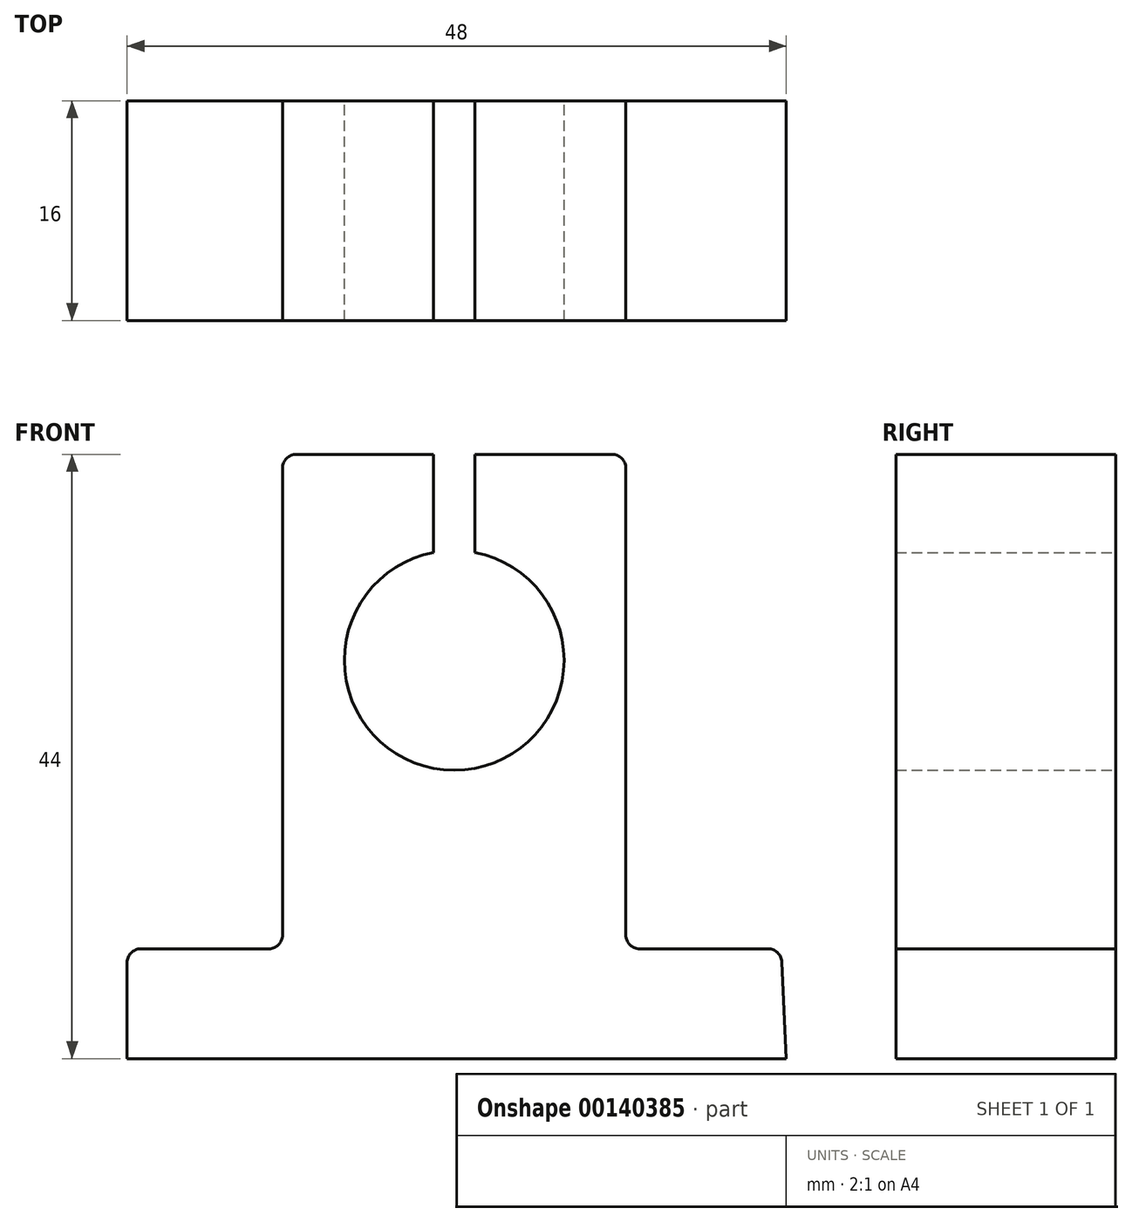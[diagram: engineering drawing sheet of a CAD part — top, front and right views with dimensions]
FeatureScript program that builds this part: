
annotation { "Feature Type Name" : "Feature", "Feature Type Description" : "" }
export const myFeature = defineFeature(function(context is Context, id is Id, definition is map)
    precondition{}
    {
        {
            var Q0;
            Q0=qCreatedBy(makeId("Front.planeOp"),FACE);
            var sketch = newSketch(context, id + "F0", { "sketchPlane" : qUnion([Q0])});
            skLineSegment(sketch, "E0", {"start": v(24.18, -11.46) * mm, "end": v(-23.82, -11.46) * mm});
            skLineSegment(sketch, "E1", {"start": v(-23.82, -11.46) * mm, "end": v(-23.82, -4.46) * mm});
            skLineSegment(sketch, "E2", {"start": v(-22.82, -3.46) * mm, "end": v(-13.5, -3.46) * mm});
            skLineSegment(sketch, "E3", {"start": v(-12.5, -2.46) * mm, "end": v(-12.5, 31.54) * mm});
            skLineSegment(sketch, "E4", {"start": v(-11.5, 32.54) * mm, "end": v(-1.5, 32.54) * mm});
            skLineSegment(sketch, "E5", {"start": v(12.5, 31.54) * mm, "end": v(12.5, -2.46) * mm});
            skLineSegment(sketch, "E6", {"start": v(13.5, -3.46) * mm, "end": v(22.86, -3.46) * mm});
            skLineSegment(sketch, "E7", {"start": v(23.86, -4.42) * mm, "end": v(24.18, -11.46) * mm});
            skPoint(sketch, "E8.visualSharp", {"position": v(-12.5, 32.54) * mm});
            skArc(sketch, "E8.filletArc", {"start": v(-11.5, 32.54) * mm, "mid": v(-12.2, 32.24) * mm, "end": v(-12.5, 31.54) * mm});
            skPoint(sketch, "E9.visualSharp", {"position": v(12.5, 32.54) * mm});
            skArc(sketch, "E9.filletArc", {"start": v(12.5, 31.54) * mm, "mid": v(12.2, 32.24) * mm, "end": v(11.5, 32.54) * mm});
            skPoint(sketch, "E10.visualSharp", {"position": v(-12.5, -3.46) * mm});
            skArc(sketch, "E10.filletArc", {"start": v(-13.5, -3.46) * mm, "mid": v(-12.8, -3.17) * mm, "end": v(-12.5, -2.46) * mm});
            skPoint(sketch, "E11.visualSharp", {"position": v(12.5, -3.46) * mm});
            skArc(sketch, "E11.filletArc", {"start": v(12.5, -2.46) * mm, "mid": v(12.8, -3.17) * mm, "end": v(13.5, -3.46) * mm});
            skArc(sketch, "E12", {"start": v(-1.5, 25.4) * mm, "mid": v(0, 9.54) * mm, "end": v(1.5, 25.4) * mm});
            skLineSegment(sketch, "E13", {"start": v(-1.5, 32.54) * mm, "end": v(-1.5, 25.4) * mm});
            skLineSegment(sketch, "E14.MirrorCS", {"start": v(1.5, 32.54) * mm, "end": v(1.5, 25.4) * mm});
            skPoint(sketch, "E15.orphan", {"position": v(-1.5, 40.72) * mm});
            skPoint(sketch, "E16.orphan", {"position": v(1.5, 40.72) * mm});
            skLineSegment(sketch, "E17.trimOffspring", {"start": v(1.5, 32.54) * mm, "end": v(11.5, 32.54) * mm});
            skLineSegment(sketch, "E18.trimOffspring", {"start": v(0, 9.54) * mm, "end": v(0, -8) * mm, "construction": true});
            skPoint(sketch, "E19.start.orphan", {"position": v(0, 24.88) * mm});
            skPoint(sketch, "E20.orphan", {"position": v(-1.5, 17.54) * mm});
            skPoint(sketch, "E21.visualSharp", {"position": v(-23.82, -3.46) * mm});
            skArc(sketch, "E21.filletArc", {"start": v(-22.82, -3.46) * mm, "mid": v(-23.53, -3.76) * mm, "end": v(-23.82, -4.46) * mm});
            skPoint(sketch, "E22.visualSharp", {"position": v(23.82, -3.46) * mm});
            skArc(sketch, "E22.filletArc", {"start": v(23.86, -4.42) * mm, "mid": v(23.56, -3.74) * mm, "end": v(22.86, -3.46) * mm});
            skSolve(sketch);
        }
        {
            var Q0;
            Q0 = qSketchRegion(id + "F0", true);
            extrude(context, id + "F1", {"entities" : qUnion([Q0]), "endBound" : BoundingType.SYMMETRIC, "depth" : 16 * mm});
        }
    });
